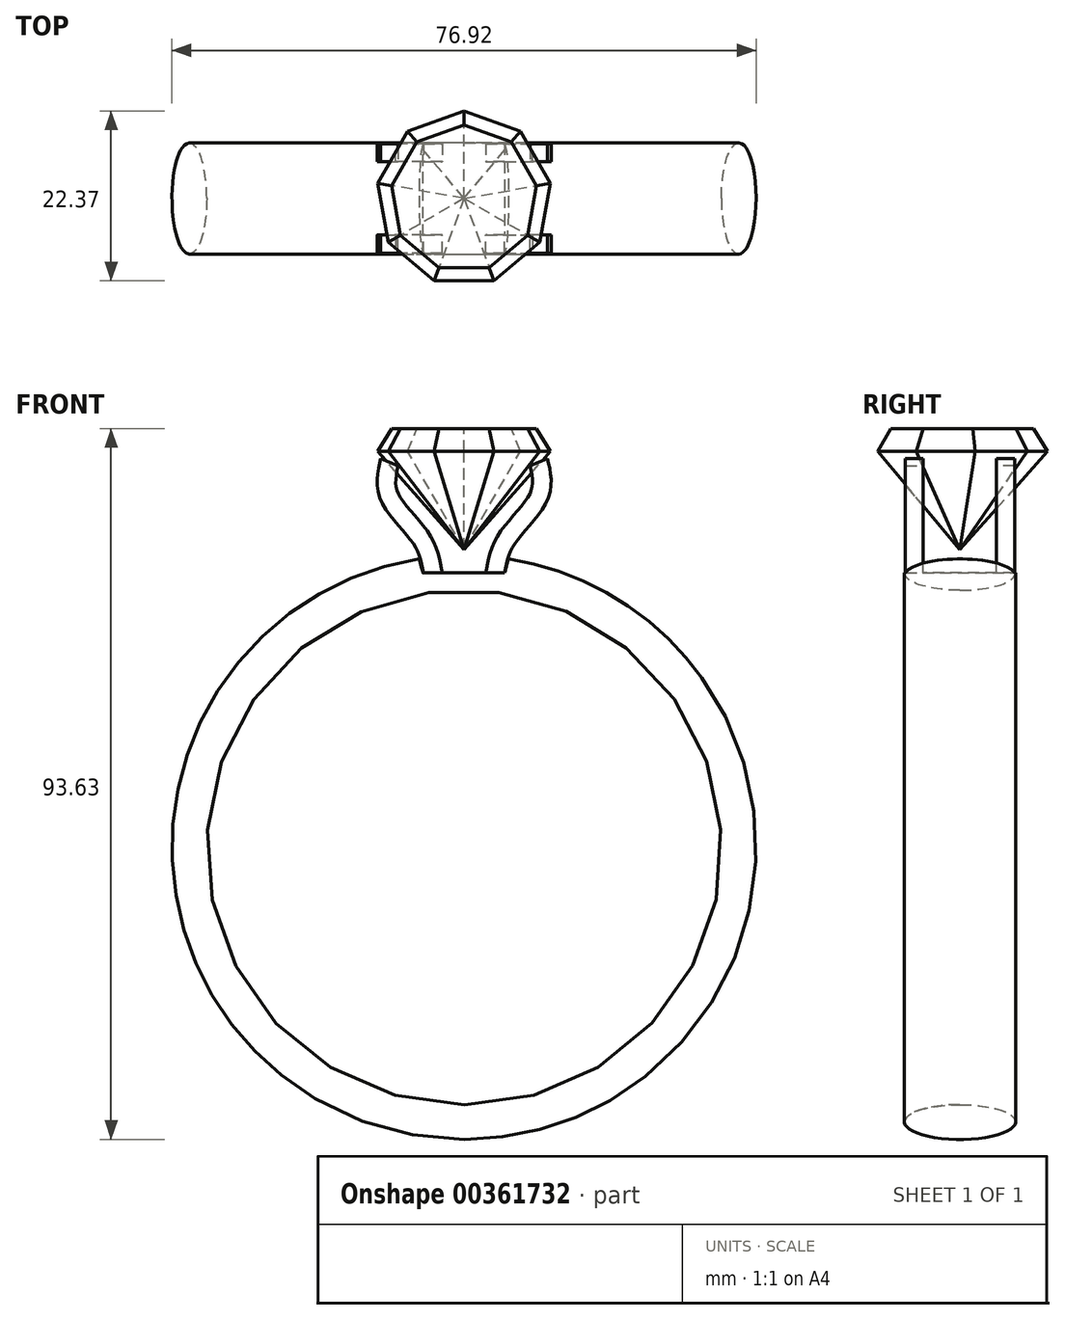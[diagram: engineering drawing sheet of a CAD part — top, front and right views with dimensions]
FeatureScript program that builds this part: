
annotation { "Feature Type Name" : "Feature", "Feature Type Description" : "" }
export const myFeature = defineFeature(function(context is Context, id is Id, definition is map)
    precondition{}
    {
        {
            var Q0;
            Q0=qCreatedBy(makeId("Right.planeOp"),FACE);
            var sketch = newSketch(context, id + "F0", { "sketchPlane" : qUnion([Q0])});
            skEllipse(sketch, "E0", {"center": v(0, 36.17) * mm, "majorRadius": 7.32 * mm, "minorRadius": 2.3 * mm, "majorAxis": v(1, 0)});
            skSolve(sketch);
        }
        {
            var Q0;
            Q0=qCreatedBy(makeId("Right.planeOp"),FACE);
            var sketch = newSketch(context, id + "F1", { "sketchPlane" : qUnion([Q0])});
            skLineSegment(sketch, "E1", {"start": v(-23.7, 0) * mm, "end": v(21.26, 0) * mm});
            skSolve(sketch);
        }
        {
            var Q0;
            Q0=makeQuery(id+"F0.imprint","IMPRINT",FACE,{"disambiguationData":[TD([[makeQuery(id+"F0.imprint","IMPRINT",EDGE,{"derivedFrom":sQuery(id+"F0.wireOp",EDGE,"E0")}),1.0]])]});
            var Q1;
            Q1=sQuery(id+"F0.wireOp",EDGE,"E0");
            var Q2;
            Q2=sQuery(id+"F1.wireOp",EDGE,"E1");
            revolve(context, id + "F2", {"entities" : qUnion([Q0]), "surfaceEntities" : qUnion([Q1]), "axis" : qUnion([Q2]), "revolveType" : RevolveType.FULL});
        }
        {
            var Q0;
            Q0=qCreatedBy(makeId("Top.planeOp"),FACE);
            var Q1;
            Q1=sQuery(id+"F0.wireOp",VERTEX,"E0.center");
            cPlane(context, id + "F3", {"entities" : qUnion([Q0, Q1]), "cplaneType" : CPlaneType.PLANE_POINT, "offset" : 100 * mm, "width" : 150 * mm, "height" : 150 * mm});
        }
        {
            var Q0;
            Q0=qCreatedBy(id+"F3.planeOp",FACE);
            var sketch = newSketch(context, id + "F4", { "sketchPlane" : qUnion([Q0])});
            skLineSegment(sketch, "E2.bottom", {"start": v(-5.43, 10.42) * mm, "end": v(5.35, 10.42) * mm});
            skLineSegment(sketch, "E2.top", {"start": v(-5.43, -11.19) * mm, "end": v(5.35, -11.19) * mm});
            skLineSegment(sketch, "E2.left", {"start": v(-5.43, 10.42) * mm, "end": v(-5.43, -11.19) * mm});
            skLineSegment(sketch, "E2.right", {"start": v(5.35, 10.42) * mm, "end": v(5.35, -11.19) * mm});
            skSolve(sketch);
        }
        {
            var Q0;
            Q0=qSketchRegion(id+"F4",true);
            extrude(context, id + "F5", {"entities" : qUnion([Q0]), "operationType" : NewBodyOperationType.REMOVE, "depth" : 5.6 * mm, "hasDraft" : true, "draftAngle" : 15 * degree});
        }
        {
            var Q0;
            Q0=qCreatedBy(id+"F3.planeOp",FACE);
            cPlane(context, id + "F6", {"entities" : qUnion([Q0]), "cplaneType" : CPlaneType.OFFSET, "offset" : 19 * mm, "width" : 150 * mm, "height" : 150 * mm});
        }
        {
            var Q0;
            Q0=qCreatedBy(id+"F6.planeOp",FACE);
            var sketch = newSketch(context, id + "F7", { "sketchPlane" : qUnion([Q0])});
            skCircle(sketch, "E3.cCircle", {"center": v(0, 0) * mm, "radius": 9.1 * mm, "construction": true});
            skLineSegment(sketch, "E3.0", {"start": v(3.31, -9.1) * mm, "end": v(-3.31, -9.1) * mm});
            skLineSegment(sketch, "E3.1", {"start": v(-3.31, -9.1) * mm, "end": v(-8.4, -4.84) * mm});
            skLineSegment(sketch, "E3.2", {"start": v(-8.4, -4.84) * mm, "end": v(-9.54, 1.68) * mm});
            skLineSegment(sketch, "E3.3", {"start": v(-9.54, 1.68) * mm, "end": v(-6.23, 7.42) * mm});
            skLineSegment(sketch, "E3.4", {"start": v(-6.23, 7.42) * mm, "end": v(0, 9.69) * mm});
            skLineSegment(sketch, "E3.5", {"start": v(0, 9.69) * mm, "end": v(6.23, 7.42) * mm});
            skLineSegment(sketch, "E3.6", {"start": v(6.23, 7.42) * mm, "end": v(9.54, 1.68) * mm});
            skLineSegment(sketch, "E3.7", {"start": v(9.54, 1.68) * mm, "end": v(8.4, -4.84) * mm});
            skLineSegment(sketch, "E3.8", {"start": v(8.4, -4.84) * mm, "end": v(3.31, -9.1) * mm});
            skPoint(sketch, "E3.0.midPoint", {"position": v(0, -9.1) * mm});
            skSolve(sketch);
        }
        {
            var Q0;
            Q0=qSketchRegion(id+"F7",true);
            extrude(context, id + "F8", {"entities" : qUnion([Q0]), "oppositeDirection" : true, "depth" : 3 * mm, "hasDraft" : true, "draftAngle" : 30 * degree});
        }
        {
            var Q0;
            Q0=makeQuery(id+"F8.opExtrude","CAP_FACE",FACE,{"disambiguationData":[OSD([sQuery(id+"F7.wireOp",EDGE,"E3.0"),sQuery(id+"F7.wireOp",EDGE,"E3.1"),sQuery(id+"F7.wireOp",EDGE,"E3.2"),sQuery(id+"F7.wireOp",EDGE,"E3.3"),sQuery(id+"F7.wireOp",EDGE,"E3.4"),sQuery(id+"F7.wireOp",EDGE,"E3.5"),sQuery(id+"F7.wireOp",EDGE,"E3.6"),sQuery(id+"F7.wireOp",EDGE,"E3.7"),sQuery(id+"F7.wireOp",EDGE,"E3.8")])],"isStart":false});
            extrude(context, id + "F9", {"entities" : qUnion([Q0]), "operationType" : NewBodyOperationType.ADD, "depth" : 21.3 * mm, "hasDraft" : true, "draftAngle" : 40 * degree, "draftPullDirection" : true});
        }
        {
            var Q0;
            Q0=makeQuery(id+"F5.boolean.opBoolean","COPY",FACE,{"derivedFrom":makeQuery(id+"F5.opExtrude","CAP_FACE",FACE,{"disambiguationData":[OSD([sQuery(id+"F4.wireOp",EDGE,"E2.bottom"),sQuery(id+"F4.wireOp",EDGE,"E2.top"),sQuery(id+"F4.wireOp",EDGE,"E2.left"),sQuery(id+"F4.wireOp",EDGE,"E2.right")])],"isStart":true})});
            var sketch = newSketch(context, id + "F10", { "sketchPlane" : qUnion([Q0])});
            skLineSegment(sketch, "E4.MirrorCS", {"start": v(-5.35, -7.2) * mm, "end": v(-5.35, -4.83) * mm});
            skLineSegment(sketch, "E5.MirrorCS", {"start": v(-5.35, -7.2) * mm, "end": v(-2.86, -7.2) * mm});
            skLineSegment(sketch, "E6.MirrorCS", {"start": v(-5.35, -4.83) * mm, "end": v(-2.86, -4.83) * mm});
            skLineSegment(sketch, "E7.MirrorCS", {"start": v(-2.86, -7.2) * mm, "end": v(-2.86, -4.83) * mm});
            skSolve(sketch);
        }
        {
            var Q0;
            Q0=qCreatedBy(makeId("Front.planeOp"),FACE);
            var sketch = newSketch(context, id + "F11", { "sketchPlane" : qUnion([Q0])});
            skPoint(sketch, "E8.0", {"position": v(-4.1, 36.17) * mm});
            skFitSpline(sketch, "E9", {"points": [v(-4.1, 36.17) * mm, v(-5.6, 40.6) * mm, v(-9.9, 46.36) * mm, v(-9.83, 50.78) * mm], "startDerivative": vector(-2.5, 14.05) * mm, "endDerivative": vector(3.34, 14.49) * mm});
            skSolve(sketch);
        }
        {
            var Q0;
            Q0=makeQuery(id+"F10.imprint","IMPRINT",FACE,{"disambiguationData":[TD([[makeQuery(id+"F10.imprint","IMPRINT",EDGE,{"derivedFrom":sQuery(id+"F10.wireOp",EDGE,"E4.MirrorCS")}),-1.0]])]});
            var Q1;
            Q1=sQuery(id+"F11.wireOp",EDGE,"E9");
            sweep(context, id + "F12", {"profiles" : qUnion([Q0]), "path" : qUnion([Q1])});
        }
        {
            var Q0;
            Q0=makeQuery(id+"F12.opSweep","SWEPT_BODY",BODY,{"disambiguationData":[OSD([sQuery(id+"F10.wireOp",EDGE,"E4.MirrorCS"),sQuery(id+"F10.wireOp",EDGE,"E5.MirrorCS"),sQuery(id+"F10.wireOp",EDGE,"E6.MirrorCS"),sQuery(id+"F10.wireOp",EDGE,"E7.MirrorCS"),sQuery(id+"F11.wireOp",EDGE,"E9")])]});
            var Q1;
            Q1=qCreatedBy(makeId("Right.planeOp"),FACE);
            mirror(context, id + "F13", {"entities" : qUnion([Q0]), "mirrorPlane" : qUnion([Q1])});
        }
        {
            var Q0;
            Q0=makeQuery(id+"F12.opSweep","SWEPT_BODY",BODY,{"disambiguationData":[OSD([sQuery(id+"F10.wireOp",EDGE,"E4.MirrorCS"),sQuery(id+"F10.wireOp",EDGE,"E5.MirrorCS"),sQuery(id+"F10.wireOp",EDGE,"E6.MirrorCS"),sQuery(id+"F10.wireOp",EDGE,"E7.MirrorCS"),sQuery(id+"F11.wireOp",EDGE,"E9")])]});
            var Q1;
            Q1=makeQuery(id+"F13.opPattern","COPY",BODY,{"derivedFrom":makeQuery(id+"F12.opSweep","SWEPT_BODY",BODY,{"disambiguationData":[OSD([sQuery(id+"F10.wireOp",EDGE,"E4.MirrorCS"),sQuery(id+"F10.wireOp",EDGE,"E5.MirrorCS"),sQuery(id+"F10.wireOp",EDGE,"E6.MirrorCS"),sQuery(id+"F10.wireOp",EDGE,"E7.MirrorCS"),sQuery(id+"F11.wireOp",EDGE,"E9")])]}),"instanceName":"1"});
            var Q2;
            Q2=qCreatedBy(makeId("Front.planeOp"),FACE);
            mirror(context, id + "F14", {"operationType" : NewBodyOperationType.ADD, "entities" : qUnion([Q0, Q1]), "mirrorPlane" : qUnion([Q2])});
        }
    });
